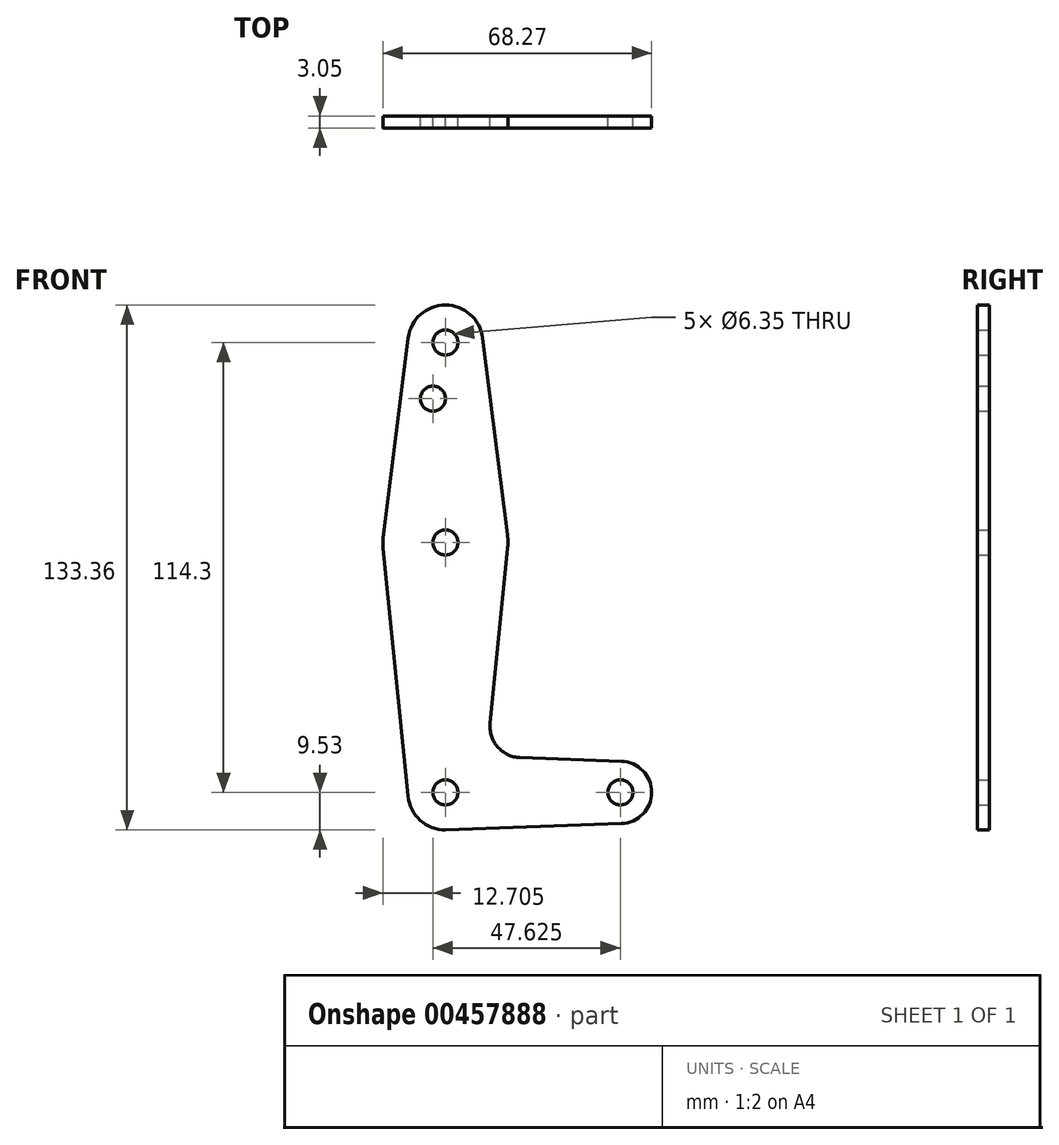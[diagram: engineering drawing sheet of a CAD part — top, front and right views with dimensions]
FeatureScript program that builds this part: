
annotation { "Feature Type Name" : "Feature", "Feature Type Description" : "" }
export const myFeature = defineFeature(function(context is Context, id is Id, definition is map)
    precondition{}
    {
        {
            var Q0;
            Q0=qCreatedBy(makeId("Front.planeOp"),FACE);
            var sketch = newSketch(context, id + "F0", { "sketchPlane" : qUnion([Q0])});
            skLineSegment(sketch, "E0", {"start": v(0, 114.3) * mm, "end": v(0, 0) * mm, "construction": true});
            skLineSegment(sketch, "E1", {"start": v(0, 0) * mm, "end": v(44.45, 0) * mm, "construction": true});
            skCircle(sketch, "E2", {"center": v(0, 114.3) * mm, "radius": 9.53 * mm});
            skCircle(sketch, "E3", {"center": v(0, 63.5) * mm, "radius": 15.88 * mm});
            skCircle(sketch, "E4", {"center": v(0, 0) * mm, "radius": 9.53 * mm});
            skCircle(sketch, "E5", {"center": v(44.45, 0) * mm, "radius": 7.94 * mm});
            skLineSegment(sketch, "E6", {"start": v(-9.45, 115.5) * mm, "end": v(-15.75, 65.48) * mm});
            skLineSegment(sketch, "E7", {"start": v(9.45, 115.5) * mm, "end": v(15.75, 65.48) * mm});
            skLineSegment(sketch, "E8", {"start": v(-15.8, 61.91) * mm, "end": v(-9.48, -0.95) * mm});
            skLineSegment(sketch, "E9", {"start": v(0, -9.53) * mm, "end": v(44.73, -7.93) * mm});
            skLineSegment(sketch, "E10.MirrorCS", {"start": v(15.8, 61.91) * mm, "end": v(11.34, 17.59) * mm});
            skLineSegment(sketch, "E11.MirrorCS", {"start": v(18.97, 8.85) * mm, "end": v(44.73, 7.93) * mm});
            skCircle(sketch, "E12", {"center": v(-3.17, 100.03) * mm, "radius": 3.18 * mm});
            skCircle(sketch, "E13", {"center": v(0, 114.3) * mm, "radius": 3.18 * mm});
            skCircle(sketch, "E14", {"center": v(0, 63.5) * mm, "radius": 3.18 * mm});
            skCircle(sketch, "E15", {"center": v(0, 0) * mm, "radius": 3.18 * mm});
            skCircle(sketch, "E16", {"center": v(44.45, 0) * mm, "radius": 3.18 * mm});
            skPoint(sketch, "E17.newPointA", {"position": v(9.48, -0.95) * mm});
            skPoint(sketch, "E17.newPointB", {"position": v(0, 9.53) * mm});
            skArc(sketch, "E17.filletArc", {"start": v(11.34, 17.59) * mm, "mid": v(13.26, 11.57) * mm, "end": v(18.97, 8.85) * mm});
            skSolve(sketch);
        }
        {
            var Q0;
            Q0=makeQuery(id+"F0.imprint","IMPRINT",FACE,{"disambiguationData":[TD([[makeQuery(id+"F0.imprint","IMPRINT",EDGE,{"derivedFrom":sQuery(id+"F0.wireOp",EDGE,"E13")}),-1.0]])]});
            var Q1;
            {var subQ1=sQuery(id+"F0.wireOp",EDGE,"E6");Q1=makeQuery(id+"F0.imprint","IMPRINT",FACE,{"disambiguationData":[TD([[makeQuery(id+"F0.imprint","IMPRINT",EDGE,{"derivedFrom":subQ1}),1.0]])]});}
            var Q2;
            Q2=makeQuery(id+"F0.imprint","IMPRINT",FACE,{"disambiguationData":[TD([[makeQuery(id+"F0.imprint","IMPRINT",EDGE,{"derivedFrom":sQuery(id+"F0.wireOp",EDGE,"E14")}),-1.0]])]});
            var Q3;
            {var subQ0=sQuery(id+"F0.wireOp",EDGE,"E8");Q3=makeQuery(id+"F0.imprint","IMPRINT",FACE,{"disambiguationData":[TD([[makeQuery(id+"F0.imprint","IMPRINT",EDGE,{"derivedFrom":subQ0}),1.0]])]});}
            var Q4;
            Q4=makeQuery(id+"F0.imprint","IMPRINT",FACE,{"disambiguationData":[TD([[makeQuery(id+"F0.imprint","IMPRINT",EDGE,{"derivedFrom":sQuery(id+"F0.wireOp",EDGE,"E15")}),-1.0]])]});
            var Q5;
            Q5=makeQuery(id+"F0.imprint","IMPRINT",FACE,{"disambiguationData":[TD([[makeQuery(id+"F0.imprint","IMPRINT",EDGE,{"derivedFrom":sQuery(id+"F0.wireOp",EDGE,"E16")}),-1.0]])]});
            extrude(context, id + "F1", {"entities" : qUnion([Q0, Q1, Q2, Q3, Q4, Q5]), "depth" : 3.05 * mm});
        }
    });
